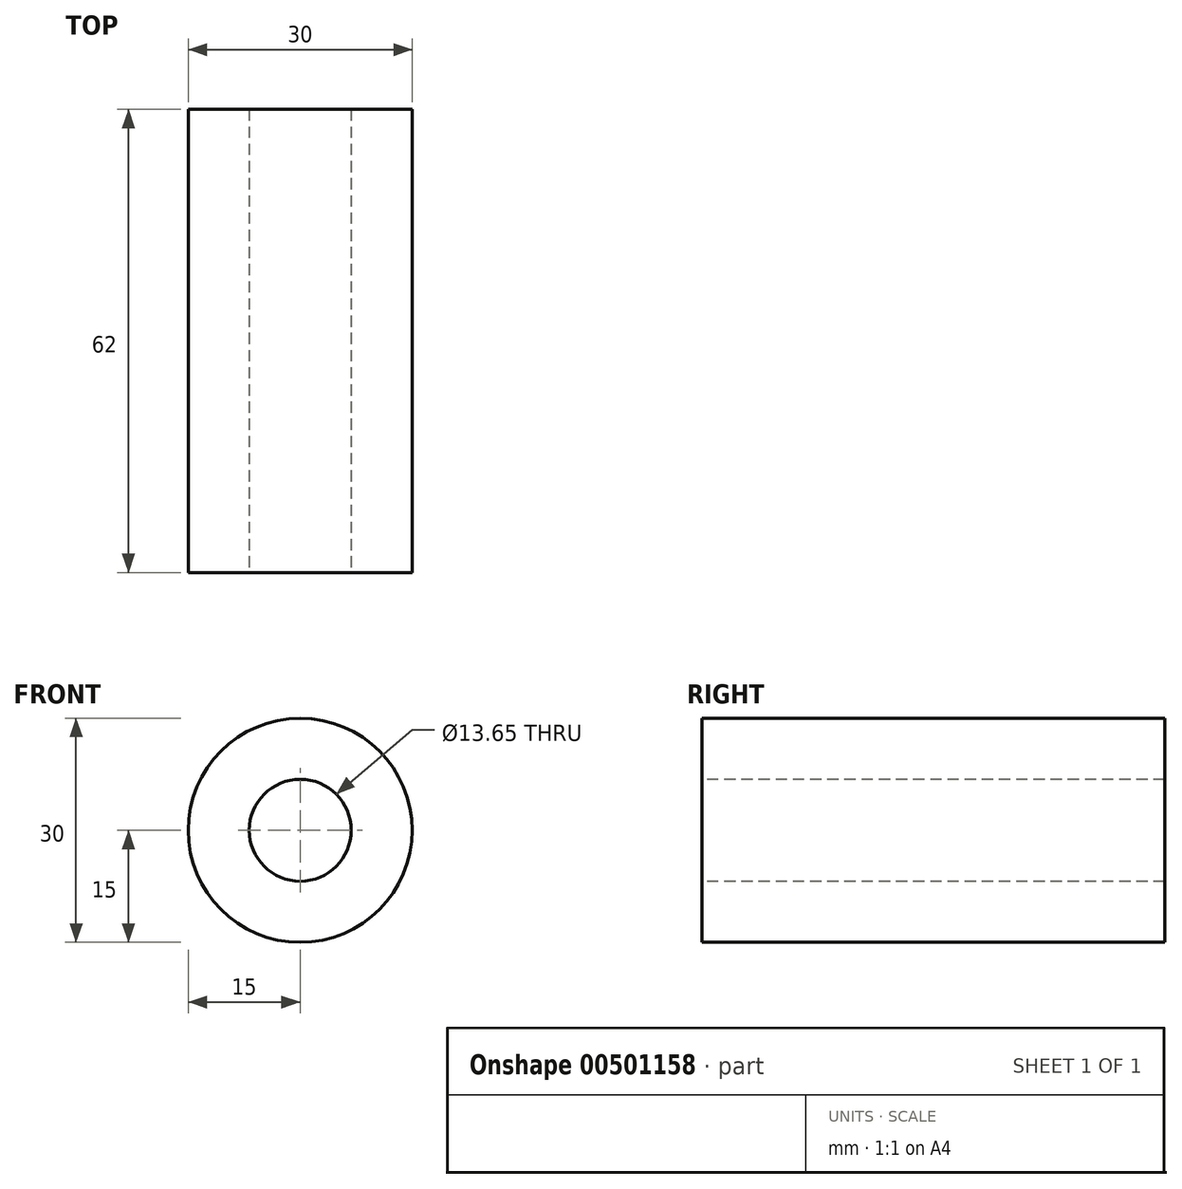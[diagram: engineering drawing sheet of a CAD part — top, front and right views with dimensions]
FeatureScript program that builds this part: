
annotation { "Feature Type Name" : "Feature", "Feature Type Description" : "" }
export const myFeature = defineFeature(function(context is Context, id is Id, definition is map)
    precondition{}
    {
        {
            var Q0;
            Q0=qCreatedBy(makeId("Front.planeOp"),FACE);
            var sketch = newSketch(context, id + "F0", { "sketchPlane" : qUnion([Q0])});
            skArc(sketch, "E0.0.startCap", {"start": v(-15, 50) * mm, "mid": v(0, 65) * mm, "end": v(15, 50) * mm});
            skLineSegment(sketch, "E0.0.left", {"start": v(15, 50) * mm, "end": v(15, 0) * mm});
            skLineSegment(sketch, "E0.0.right", {"start": v(-15, 50) * mm, "end": v(-15, 0) * mm});
            skCircle(sketch, "E1", {"center": v(0, 50) * mm, "radius": 6.82 * mm});
            skCircle(sketch, "E2", {"center": v(0, 0) * mm, "radius": 6.82 * mm});
            skCircle(sketch, "E3.converted", {"center": v(0, 0) * mm, "radius": 15 * mm});
            skSolve(sketch);
        }
        {
            var Q0;
            Q0=makeQuery(id+"F0.imprint","IMPRINT",FACE,{"disambiguationData":[TD([[makeQuery(id+"F0.imprint","IMPRINT",EDGE,{"derivedFrom":sQuery(id+"F0.wireOp",EDGE,"E0.0.startCap")}),-1.0]])]});
            var Q1;
            Q1=makeQuery(id+"F0.imprint","IMPRINT",FACE,{"disambiguationData":[TD([[makeQuery(id+"F0.imprint","IMPRINT",EDGE,{"derivedFrom":sQuery(id+"F0.wireOp",EDGE,"E2")}),-1.0]])]});
            extrude(context, id + "F1", {"entities" : qUnion([Q0, Q1]), "oppositeDirection" : true, "depth" : 12 * mm});
        }
        {
            var Q0;
            Q0=makeQuery(id+"F0.imprint","IMPRINT",FACE,{"disambiguationData":[TD([[makeQuery(id+"F0.imprint","IMPRINT",EDGE,{"derivedFrom":sQuery(id+"F0.wireOp",EDGE,"E2")}),-1.0]])]});
            extrude(context, id + "F2", {"entities" : qUnion([Q0]), "operationType" : NewBodyOperationType.ADD, "oppositeDirection" : true, "depth" : 31 * mm});
        }
        {
            var Q0;
            Q0=makeQuery(id+"F1.opExtrude","SWEPT_BODY",BODY,{"disambiguationData":[OSD([sQuery(id+"F0.wireOp",EDGE,"E0.0.startCap"),sQuery(id+"F0.wireOp",EDGE,"E0.0.left"),sQuery(id+"F0.wireOp",EDGE,"E0.0.right"),sQuery(id+"F0.wireOp",EDGE,"E1"),sQuery(id+"F0.wireOp",EDGE,"E2"),sQuery(id+"F0.wireOp",EDGE,"E3.converted")])]});
            var Q1;
            Q1=makeQuery(id+"F2.opExtrude","CAP_FACE",FACE,{"disambiguationData":[OSD([sQuery(id+"F0.wireOp",EDGE,"E2"),sQuery(id+"F0.wireOp",EDGE,"E3.converted")])],"isStart":false});
            mirror(context, id + "F3", {"operationType" : NewBodyOperationType.ADD, "entities" : qUnion([Q0]), "mirrorPlane" : qUnion([Q1])});
        }
    });
